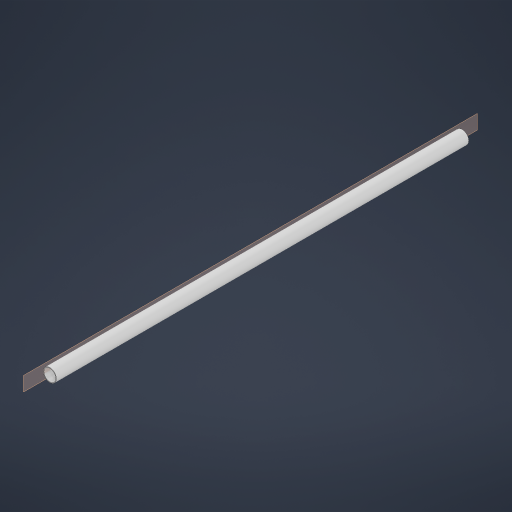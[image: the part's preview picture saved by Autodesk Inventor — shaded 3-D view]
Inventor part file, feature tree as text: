
AUTODESK INVENTOR PART (.ipt)
format: ipt  version: 2024 (Build 280153000, 153)  size: 190,464 bytes
history: native  units: mm
features: extrude x2, sketch x2, other x1, plane x1
ambient origin geometry x8: Origin, YZ Plane, XZ Plane, XY Plane, X Axis, Y Axis, Z Axis, Center Point
bodies: Body1 (feature_tree)
feature tree (6):
  other  "Sólido1"
  extrude  "Extrusión1"  Depth=170.62mm
  plane  "Plano de trabajo3"
  extrude  "Extrusión3"  [1 undecoded]
  sketch  "Boceto1"  dims[d0=190.0mm d1=170.62mm]
  sketch  "Boceto4"  dims[d2=6000.0mm d3=0.0mm d9=-81.25mm d11=105.0mm d12=60.0mm d13=0.0mm d6=0.5mm d7=0.872665mm d8=0.5mm]
note: 1 required parameter value undecoded (feature->parameter linkage not recoverable at this tier; creation-order binding heuristic only, values carry confidence <= 0.55)
